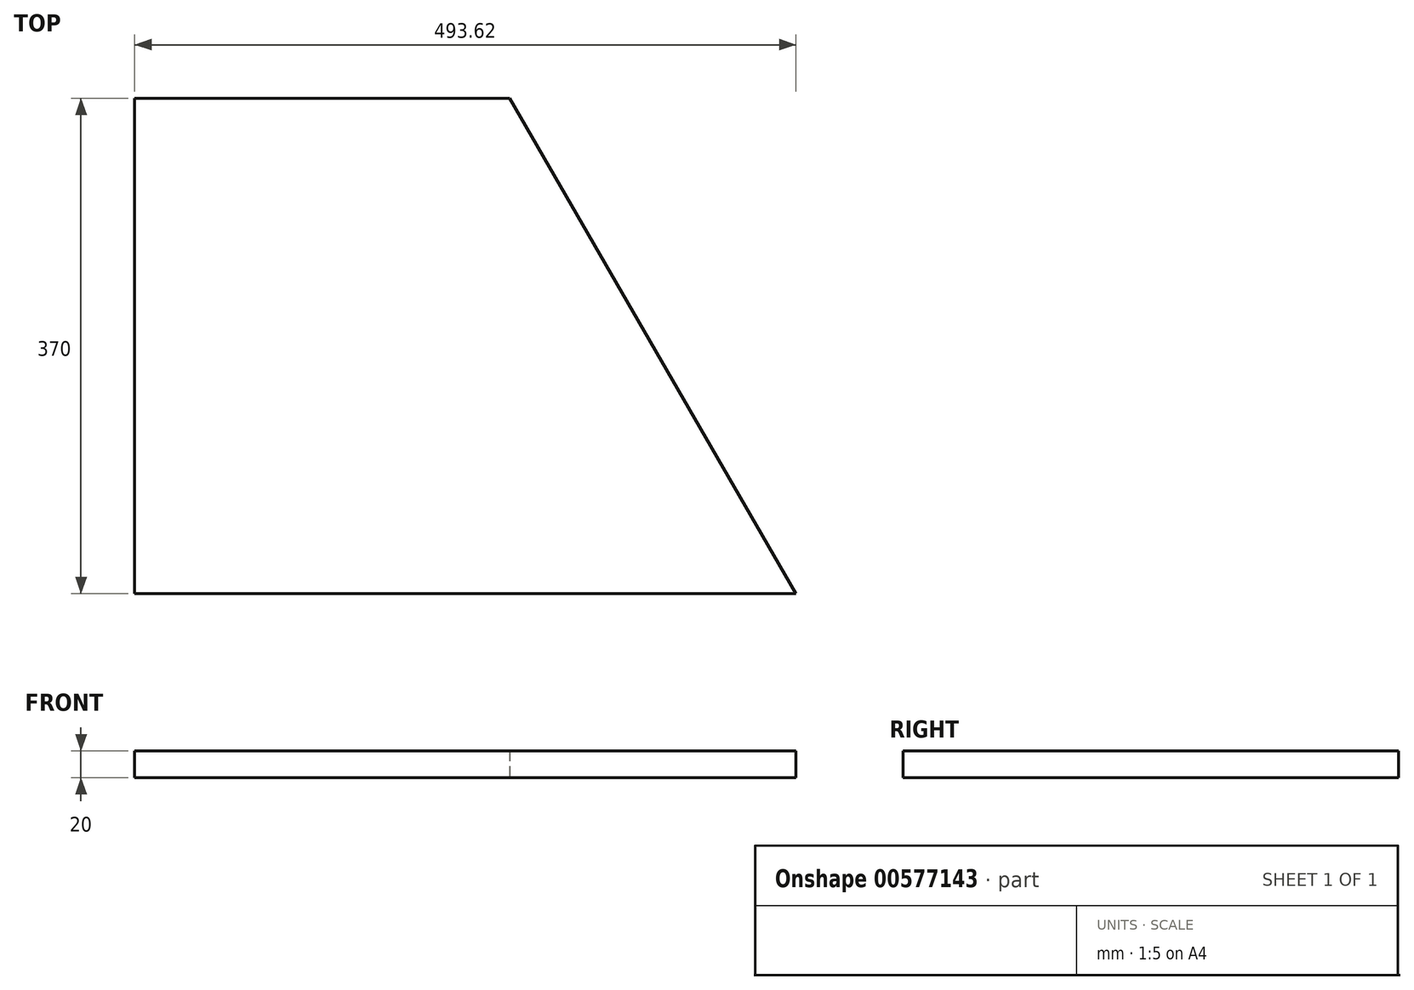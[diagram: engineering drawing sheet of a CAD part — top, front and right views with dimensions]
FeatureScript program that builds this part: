
annotation { "Feature Type Name" : "Feature", "Feature Type Description" : "" }
export const myFeature = defineFeature(function(context is Context, id is Id, definition is map)
    precondition{}
    {
        {
            var Q0;
            Q0=qCreatedBy(makeId("Top.planeOp"),FACE);
            var sketch = newSketch(context, id + "F0", { "sketchPlane" : qUnion([Q0])});
            skLineSegment(sketch, "E0.left", {"start": v(-280, 185) * mm, "end": v(-280, -185) * mm});
            skPoint(sketch, "E0.middle", {"position": v(0, 0) * mm});
            skLineSegment(sketch, "E1", {"start": v(-280, 185) * mm, "end": v(0, 185) * mm});
            skLineSegment(sketch, "E2", {"start": v(-280, -185) * mm, "end": v(213.62, -185) * mm});
            skLineSegment(sketch, "E3", {"start": v(213.62, -185) * mm, "end": v(0, 185) * mm});
            skSolve(sketch);
        }
        {
            var Q0;
            Q0 = qSketchRegion(id + "F0", true);
            extrude(context, id + "F1", {"entities" : qUnion([Q0]), "depth" : 20 * mm, "offsetDistance" : 25 * mm});
        }
    });
